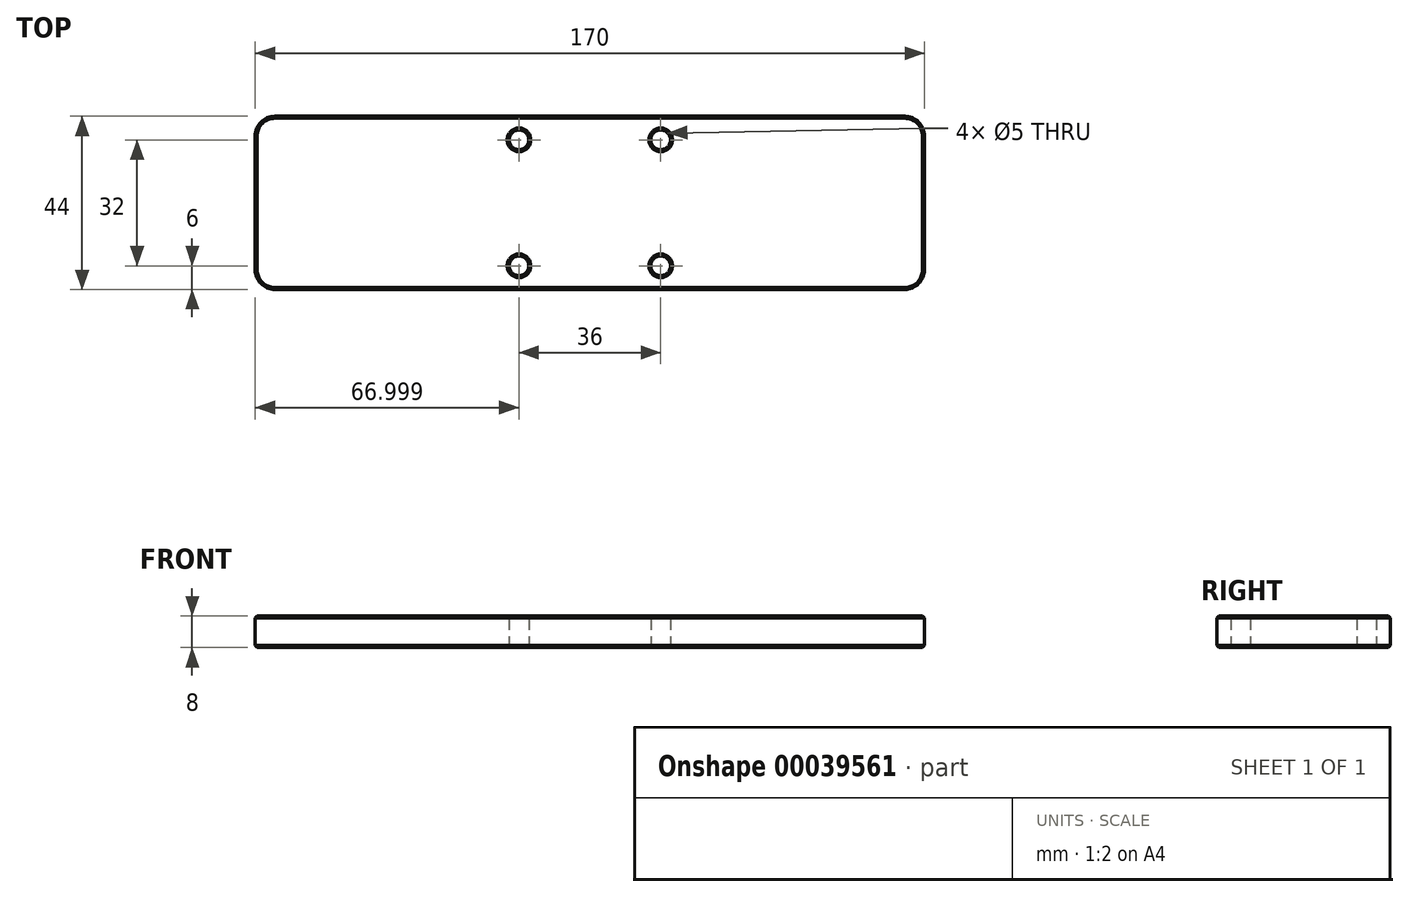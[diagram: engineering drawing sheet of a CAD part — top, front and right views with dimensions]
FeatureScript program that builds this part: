
annotation { "Feature Type Name" : "Feature", "Feature Type Description" : "" }
export const myFeature = defineFeature(function(context is Context, id is Id, definition is map)
    precondition{}
    {
        {
            var Q0;
            Q0=qCreatedBy(makeId("Top.planeOp"),FACE);
            var sketch = newSketch(context, id + "F0", { "sketchPlane" : qUnion([Q0])});
            skLineSegment(sketch, "E0.bottom", {"start": v(35.96, -34.6) * mm, "end": v(205.96, -34.6) * mm});
            skLineSegment(sketch, "E0.top", {"start": v(35.96, 9.4) * mm, "end": v(205.96, 9.4) * mm});
            skLineSegment(sketch, "E0.left", {"start": v(35.96, -34.6) * mm, "end": v(35.96, 9.4) * mm});
            skLineSegment(sketch, "E0.right", {"start": v(205.96, -34.6) * mm, "end": v(205.96, 9.4) * mm});
            skCircle(sketch, "E1", {"center": v(102.96, 3.4) * mm, "radius": 2.5 * mm});
            skCircle(sketch, "E2", {"center": v(138.96, 3.4) * mm, "radius": 2.5 * mm});
            skCircle(sketch, "E3", {"center": v(138.96, -28.6) * mm, "radius": 2.5 * mm});
            skCircle(sketch, "E4", {"center": v(102.96, -28.6) * mm, "radius": 2.5 * mm});
            skSolve(sketch);
        }
        {
            var Q0;
            Q0=makeQuery(id+"F0.imprint","IMPRINT",FACE,{"disambiguationData":[TD([[makeQuery(id+"F0.imprint","IMPRINT",EDGE,{"derivedFrom":sQuery(id+"F0.wireOp",EDGE,"E0.bottom")}),1.0]])]});
            extrude(context, id + "F1", {"entities" : qUnion([Q0]), "depth" : 8 * mm});
        }
        {
            var Q0;
            Q0=makeQuery(id+"F1.opExtrude","SWEPT_EDGE",EDGE,{"disambiguationData":[OSD([sQuery(id+"F0.wireOp",EDGE,"E0.bottom"),sQuery(id+"F0.wireOp",EDGE,"E0.left")])]});
            var Q1;
            Q1=makeQuery(id+"F1.opExtrude","SWEPT_EDGE",EDGE,{"disambiguationData":[OSD([sQuery(id+"F0.wireOp",EDGE,"E0.bottom"),sQuery(id+"F0.wireOp",EDGE,"E0.right")])]});
            var Q2;
            Q2=makeQuery(id+"F1.opExtrude","SWEPT_EDGE",EDGE,{"disambiguationData":[OSD([sQuery(id+"F0.wireOp",EDGE,"E0.top"),sQuery(id+"F0.wireOp",EDGE,"E0.right")])]});
            var Q3;
            Q3=makeQuery(id+"F1.opExtrude","SWEPT_EDGE",EDGE,{"disambiguationData":[OSD([sQuery(id+"F0.wireOp",EDGE,"E0.top"),sQuery(id+"F0.wireOp",EDGE,"E0.left")])]});
            fillet(context, id + "F2", {"entities" : qUnion([Q0, Q1, Q2, Q3]), "radius" : 5 * mm, "tangentPropagation" : true, "allowEdgeOverflow" : false});
        }
        {
            var Q0;
            Q0=makeQuery(id+"F1.opExtrude","CAP_EDGE",EDGE,{"disambiguationData":[OSD([sQuery(id+"F0.wireOp",EDGE,"E0.bottom")])],"isStart":false});
            var Q1;
            Q1=makeQuery(id+"F1.opExtrude","CAP_EDGE",EDGE,{"disambiguationData":[OSD([sQuery(id+"F0.wireOp",EDGE,"E0.bottom")])],"isStart":true});
            var Q2;
            Q2=makeQuery(id+"F1.opExtrude","CAP_EDGE",EDGE,{"disambiguationData":[OSD([sQuery(id+"F0.wireOp",EDGE,"E3")])],"isStart":false});
            var Q3;
            {var subQ0=sQuery(id+"F0.wireOp",EDGE,"E0.bottom");var subQ1=sQuery(id+"F0.wireOp",EDGE,"E0.right");Q3=makeQuery(id+"F2.opFillet","BLEND_EDGE",EDGE,{"blendedFrom":[makeQuery(id+"F1.opExtrude","SWEPT_EDGE",EDGE,{"disambiguationData":[OSD([subQ0,subQ1])]}),makeQuery(id+"F1.opExtrude","CAP_FACE",FACE,{"disambiguationData":[OSD([subQ0,sQuery(id+"F0.wireOp",EDGE,"E0.top"),sQuery(id+"F0.wireOp",EDGE,"E0.left"),subQ1,sQuery(id+"F0.wireOp",EDGE,"E1"),sQuery(id+"F0.wireOp",EDGE,"E2"),sQuery(id+"F0.wireOp",EDGE,"E3"),sQuery(id+"F0.wireOp",EDGE,"E4")])],"isStart":false})],"blendedInto":[makeQuery(id+"F1.opExtrude","CAP_FACE",FACE,{"disambiguationData":[OSD([subQ0,sQuery(id+"F0.wireOp",EDGE,"E0.top"),sQuery(id+"F0.wireOp",EDGE,"E0.left"),subQ1,sQuery(id+"F0.wireOp",EDGE,"E1"),sQuery(id+"F0.wireOp",EDGE,"E2"),sQuery(id+"F0.wireOp",EDGE,"E3"),sQuery(id+"F0.wireOp",EDGE,"E4")])],"isStart":false})]});}
            var Q4;
            Q4=makeQuery(id+"F1.opExtrude","CAP_EDGE",EDGE,{"disambiguationData":[OSD([sQuery(id+"F0.wireOp",EDGE,"E0.right")])],"isStart":false});
            var Q5;
            {var subQ0=sQuery(id+"F0.wireOp",EDGE,"E0.top");var subQ1=sQuery(id+"F0.wireOp",EDGE,"E0.right");Q5=makeQuery(id+"F2.opFillet","BLEND_EDGE",EDGE,{"blendedFrom":[makeQuery(id+"F1.opExtrude","SWEPT_EDGE",EDGE,{"disambiguationData":[OSD([subQ0,subQ1])]}),makeQuery(id+"F1.opExtrude","CAP_FACE",FACE,{"disambiguationData":[OSD([sQuery(id+"F0.wireOp",EDGE,"E0.bottom"),subQ0,sQuery(id+"F0.wireOp",EDGE,"E0.left"),subQ1,sQuery(id+"F0.wireOp",EDGE,"E1"),sQuery(id+"F0.wireOp",EDGE,"E2"),sQuery(id+"F0.wireOp",EDGE,"E3"),sQuery(id+"F0.wireOp",EDGE,"E4")])],"isStart":false})],"blendedInto":[makeQuery(id+"F1.opExtrude","CAP_FACE",FACE,{"disambiguationData":[OSD([sQuery(id+"F0.wireOp",EDGE,"E0.bottom"),subQ0,sQuery(id+"F0.wireOp",EDGE,"E0.left"),subQ1,sQuery(id+"F0.wireOp",EDGE,"E1"),sQuery(id+"F0.wireOp",EDGE,"E2"),sQuery(id+"F0.wireOp",EDGE,"E3"),sQuery(id+"F0.wireOp",EDGE,"E4")])],"isStart":false})]});}
            var Q6;
            Q6=makeQuery(id+"F1.opExtrude","CAP_EDGE",EDGE,{"disambiguationData":[OSD([sQuery(id+"F0.wireOp",EDGE,"E0.top")])],"isStart":false});
            var Q7;
            {var subQ0=sQuery(id+"F0.wireOp",EDGE,"E0.top");var subQ1=sQuery(id+"F0.wireOp",EDGE,"E0.left");Q7=makeQuery(id+"F2.opFillet","BLEND_EDGE",EDGE,{"blendedFrom":[makeQuery(id+"F1.opExtrude","SWEPT_EDGE",EDGE,{"disambiguationData":[OSD([subQ0,subQ1])]}),makeQuery(id+"F1.opExtrude","CAP_FACE",FACE,{"disambiguationData":[OSD([sQuery(id+"F0.wireOp",EDGE,"E0.bottom"),subQ0,subQ1,sQuery(id+"F0.wireOp",EDGE,"E0.right"),sQuery(id+"F0.wireOp",EDGE,"E1"),sQuery(id+"F0.wireOp",EDGE,"E2"),sQuery(id+"F0.wireOp",EDGE,"E3"),sQuery(id+"F0.wireOp",EDGE,"E4")])],"isStart":false})],"blendedInto":[makeQuery(id+"F1.opExtrude","CAP_FACE",FACE,{"disambiguationData":[OSD([sQuery(id+"F0.wireOp",EDGE,"E0.bottom"),subQ0,subQ1,sQuery(id+"F0.wireOp",EDGE,"E0.right"),sQuery(id+"F0.wireOp",EDGE,"E1"),sQuery(id+"F0.wireOp",EDGE,"E2"),sQuery(id+"F0.wireOp",EDGE,"E3"),sQuery(id+"F0.wireOp",EDGE,"E4")])],"isStart":false})]});}
            var Q8;
            Q8=makeQuery(id+"F1.opExtrude","CAP_EDGE",EDGE,{"disambiguationData":[OSD([sQuery(id+"F0.wireOp",EDGE,"E0.left")])],"isStart":false});
            var Q9;
            {var subQ0=sQuery(id+"F0.wireOp",EDGE,"E0.bottom");var subQ1=sQuery(id+"F0.wireOp",EDGE,"E0.left");Q9=makeQuery(id+"F2.opFillet","BLEND_EDGE",EDGE,{"blendedFrom":[makeQuery(id+"F1.opExtrude","SWEPT_EDGE",EDGE,{"disambiguationData":[OSD([subQ0,subQ1])]}),makeQuery(id+"F1.opExtrude","CAP_FACE",FACE,{"disambiguationData":[OSD([subQ0,sQuery(id+"F0.wireOp",EDGE,"E0.top"),subQ1,sQuery(id+"F0.wireOp",EDGE,"E0.right"),sQuery(id+"F0.wireOp",EDGE,"E1"),sQuery(id+"F0.wireOp",EDGE,"E2"),sQuery(id+"F0.wireOp",EDGE,"E3"),sQuery(id+"F0.wireOp",EDGE,"E4")])],"isStart":false})],"blendedInto":[makeQuery(id+"F1.opExtrude","CAP_FACE",FACE,{"disambiguationData":[OSD([subQ0,sQuery(id+"F0.wireOp",EDGE,"E0.top"),subQ1,sQuery(id+"F0.wireOp",EDGE,"E0.right"),sQuery(id+"F0.wireOp",EDGE,"E1"),sQuery(id+"F0.wireOp",EDGE,"E2"),sQuery(id+"F0.wireOp",EDGE,"E3"),sQuery(id+"F0.wireOp",EDGE,"E4")])],"isStart":false})]});}
            var Q10;
            Q10=makeQuery(id+"F1.opExtrude","CAP_EDGE",EDGE,{"disambiguationData":[OSD([sQuery(id+"F0.wireOp",EDGE,"E4")])],"isStart":false});
            var Q11;
            Q11=makeQuery(id+"F1.opExtrude","CAP_EDGE",EDGE,{"disambiguationData":[OSD([sQuery(id+"F0.wireOp",EDGE,"E1")])],"isStart":false});
            var Q12;
            Q12=makeQuery(id+"F1.opExtrude","CAP_EDGE",EDGE,{"disambiguationData":[OSD([sQuery(id+"F0.wireOp",EDGE,"E2")])],"isStart":false});
            var Q13;
            Q13=makeQuery(id+"F1.opExtrude","CAP_EDGE",EDGE,{"disambiguationData":[OSD([sQuery(id+"F0.wireOp",EDGE,"E3")])],"isStart":true});
            var Q14;
            Q14=makeQuery(id+"F1.opExtrude","CAP_EDGE",EDGE,{"disambiguationData":[OSD([sQuery(id+"F0.wireOp",EDGE,"E2")])],"isStart":true});
            var Q15;
            Q15=makeQuery(id+"F1.opExtrude","CAP_EDGE",EDGE,{"disambiguationData":[OSD([sQuery(id+"F0.wireOp",EDGE,"E1")])],"isStart":true});
            var Q16;
            Q16=makeQuery(id+"F1.opExtrude","CAP_EDGE",EDGE,{"disambiguationData":[OSD([sQuery(id+"F0.wireOp",EDGE,"E4")])],"isStart":true});
            chamfer(context, id + "F3", {"entities" : qUnion([Q0, Q1, Q2, Q3, Q4, Q5, Q6, Q7, Q8, Q9, Q10, Q11, Q12, Q13, Q14, Q15, Q16]), "width" : 0.5 * mm, "tangentPropagation" : true});
        }
    });
